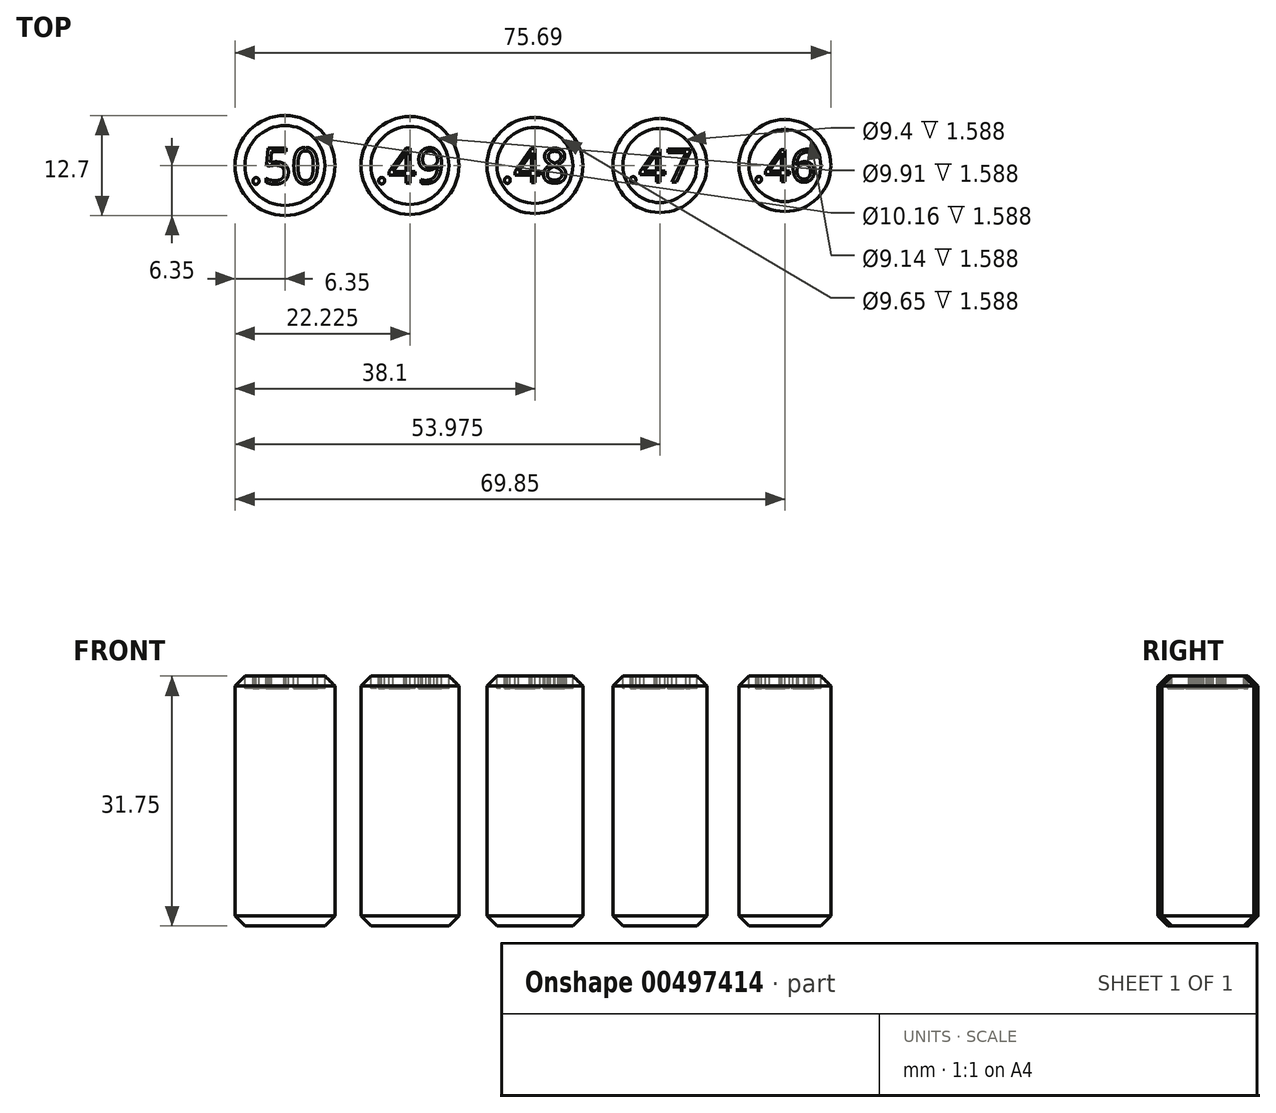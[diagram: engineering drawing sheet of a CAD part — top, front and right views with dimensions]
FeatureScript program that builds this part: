
annotation { "Feature Type Name" : "Feature", "Feature Type Description" : "" }
export const myFeature = defineFeature(function(context is Context, id is Id, definition is map)
    precondition{}
    {
        {
            var Q0;
            Q0=qCreatedBy(makeId("Top.planeOp"),FACE);
            var sketch = newSketch(context, id + "F0", { "sketchPlane" : qUnion([Q0])});
            skCircle(sketch, "E0", {"center": v(-31.75, 0) * mm, "radius": 6.35 * mm});
            skCircle(sketch, "E1", {"center": v(-15.88, 0) * mm, "radius": 6.22 * mm});
            skCircle(sketch, "E2", {"center": v(0, 0) * mm, "radius": 6.1 * mm});
            skCircle(sketch, "E3", {"center": v(15.88, 0) * mm, "radius": 5.97 * mm});
            skCircle(sketch, "E4", {"center": v(31.75, 0) * mm, "radius": 5.84 * mm});
            skSolve(sketch);
        }
        {
            var Q0;
            Q0=makeQuery(id+"F0.imprint","IMPRINT",FACE,{"disambiguationData":[TD([[makeQuery(id+"F0.imprint","IMPRINT",EDGE,{"derivedFrom":sQuery(id+"F0.wireOp",EDGE,"E0")}),1.0]])]});
            var Q1;
            Q1=makeQuery(id+"F0.imprint","IMPRINT",FACE,{"disambiguationData":[TD([[makeQuery(id+"F0.imprint","IMPRINT",EDGE,{"derivedFrom":sQuery(id+"F0.wireOp",EDGE,"E1")}),1.0]])]});
            var Q2;
            Q2=makeQuery(id+"F0.imprint","IMPRINT",FACE,{"disambiguationData":[TD([[makeQuery(id+"F0.imprint","IMPRINT",EDGE,{"derivedFrom":sQuery(id+"F0.wireOp",EDGE,"E2")}),1.0]])]});
            var Q3;
            Q3=makeQuery(id+"F0.imprint","IMPRINT",FACE,{"disambiguationData":[TD([[makeQuery(id+"F0.imprint","IMPRINT",EDGE,{"derivedFrom":sQuery(id+"F0.wireOp",EDGE,"E3")}),1.0]])]});
            var Q4;
            Q4=makeQuery(id+"F0.imprint","IMPRINT",FACE,{"disambiguationData":[TD([[makeQuery(id+"F0.imprint","IMPRINT",EDGE,{"derivedFrom":sQuery(id+"F0.wireOp",EDGE,"E4")}),1.0]])]});
            extrude(context, id + "F1", {"entities" : qUnion([Q0, Q1, Q2, Q3, Q4]), "depth" : 31.75 * mm});
        }
        {
            var Q0;
            Q0=makeQuery(id+"F1.opExtrude","SWEPT_FACE",FACE,{"disambiguationData":[OSD([sQuery(id+"F0.wireOp",EDGE,"E0")])]});
            var Q1;
            Q1=makeQuery(id+"F1.opExtrude","SWEPT_FACE",FACE,{"disambiguationData":[OSD([sQuery(id+"F0.wireOp",EDGE,"E1")])]});
            var Q2;
            Q2=makeQuery(id+"F1.opExtrude","SWEPT_FACE",FACE,{"disambiguationData":[OSD([sQuery(id+"F0.wireOp",EDGE,"E2")])]});
            var Q3;
            Q3=makeQuery(id+"F1.opExtrude","SWEPT_FACE",FACE,{"disambiguationData":[OSD([sQuery(id+"F0.wireOp",EDGE,"E3")])]});
            var Q4;
            Q4=makeQuery(id+"F1.opExtrude","SWEPT_FACE",FACE,{"disambiguationData":[OSD([sQuery(id+"F0.wireOp",EDGE,"E4")])]});
            chamfer(context, id + "F2", {"entities" : qUnion([Q0, Q1, Q2, Q3, Q4]), "width" : 1.27 * mm, "tangentPropagation" : true});
        }
        {
            var Q0;
            Q0=makeQuery(id+"F1.opExtrude","CAP_FACE",FACE,{"disambiguationData":[OSD([sQuery(id+"F0.wireOp",EDGE,"E0")])],"isStart":false});
            var sketch = newSketch(context, id + "F3", { "sketchPlane" : qUnion([Q0])});
            skText(sketch, "E5", { "text": ".50", "fontName": "OpenSans-Regular.ttf"});
            skCircle(sketch, "E6.0", {"center": v(-15.88, 0) * mm, "radius": 4.95 * mm});
            skCircle(sketch, "E7.0", {"center": v(-31.75, 0) * mm, "radius": 5.08 * mm});
            skCircle(sketch, "E8.0", {"center": v(0, 0) * mm, "radius": 4.83 * mm});
            skCircle(sketch, "E9.0", {"center": v(15.88, 0) * mm, "radius": 4.7 * mm});
            skCircle(sketch, "E10.0", {"center": v(31.75, 0) * mm, "radius": 4.57 * mm});
            skText(sketch, "E11", { "text": ".49", "fontName": "OpenSans-Regular.ttf"});
            skText(sketch, "E12", { "text": ".48", "fontName": "OpenSans-Regular.ttf"});
            skText(sketch, "E13", { "text": ".47", "fontName": "OpenSans-Regular.ttf"});
            skText(sketch, "E14", { "text": ".46", "fontName": "OpenSans-Regular.ttf"});
            const initialGuessF3  = {"E5": [-0.03628, -0.0023, 1, 0, 0.00458], "E11": [-0.0203, -0.00224, 1, 0, 0.00448], "E12": [-0.0043, -0.00218, 1, 0, 0.00436], "E13": [0.01168, -0.00212, 1, 0, 0.00424], "E14": [0.02767, -0.00206, 1, 0, 0.00412]};
            skSetInitialGuess(sketch, initialGuessF3);
            skSolve(sketch);
        }
        {
            var Q0;
            Q0=makeQuery(id+"F3.imprint","IMPRINT",FACE,{"disambiguationData":[TD([[makeQuery(id+"F3.imprint","IMPRINT",EDGE,{"derivedFrom":sQuery(id+"F3.wireOp",EDGE,"E5.sketch_text.stroke-0")}),1.0]])]});
            var Q1;
            Q1=makeQuery(id+"F3.imprint","IMPRINT",FACE,{"disambiguationData":[TD([[makeQuery(id+"F3.imprint","IMPRINT",EDGE,{"derivedFrom":sQuery(id+"F3.wireOp",EDGE,"E5.sketch_text.stroke-35")}),1.0]])]});
            var Q2;
            Q2=makeQuery(id+"F3.imprint","IMPRINT",FACE,{"disambiguationData":[TD([[makeQuery(id+"F3.imprint","IMPRINT",EDGE,{"derivedFrom":sQuery(id+"F3.wireOp",EDGE,"E6.0")}),1.0]])]});
            var Q3;
            Q3=makeQuery(id+"F3.imprint","IMPRINT",FACE,{"disambiguationData":[TD([[makeQuery(id+"F3.imprint","IMPRINT",EDGE,{"derivedFrom":sQuery(id+"F3.wireOp",EDGE,"E8.0")}),1.0]])]});
            var Q4;
            Q4=makeQuery(id+"F3.imprint","IMPRINT",FACE,{"disambiguationData":[TD([[makeQuery(id+"F3.imprint","IMPRINT",EDGE,{"derivedFrom":sQuery(id+"F3.wireOp",EDGE,"E9.0")}),1.0]])]});
            var Q5;
            Q5=makeQuery(id+"F3.imprint","IMPRINT",FACE,{"disambiguationData":[TD([[makeQuery(id+"F3.imprint","IMPRINT",EDGE,{"derivedFrom":sQuery(id+"F3.wireOp",EDGE,"E10.0")}),1.0]])]});
            var Q6;
            Q6=makeQuery(id+"F3.imprint","IMPRINT",FACE,{"disambiguationData":[TD([[makeQuery(id+"F3.imprint","IMPRINT",EDGE,{"derivedFrom":sQuery(id+"F3.wireOp",EDGE,"E14.sketch_text.stroke-40")}),1.0]])]});
            var Q7;
            Q7=makeQuery(id+"F3.imprint","IMPRINT",FACE,{"disambiguationData":[TD([[makeQuery(id+"F3.imprint","IMPRINT",EDGE,{"derivedFrom":sQuery(id+"F3.wireOp",EDGE,"E14.sketch_text.stroke-19")}),1.0]])]});
            var Q8;
            Q8=makeQuery(id+"F3.imprint","IMPRINT",FACE,{"disambiguationData":[TD([[makeQuery(id+"F3.imprint","IMPRINT",EDGE,{"derivedFrom":sQuery(id+"F3.wireOp",EDGE,"E13.sketch_text.stroke-19")}),1.0]])]});
            var Q9;
            Q9=makeQuery(id+"F3.imprint","IMPRINT",FACE,{"disambiguationData":[TD([[makeQuery(id+"F3.imprint","IMPRINT",EDGE,{"derivedFrom":sQuery(id+"F3.wireOp",EDGE,"E12.sketch_text.stroke-40")}),1.0]])]});
            var Q10;
            Q10=makeQuery(id+"F3.imprint","IMPRINT",FACE,{"disambiguationData":[TD([[makeQuery(id+"F3.imprint","IMPRINT",EDGE,{"derivedFrom":sQuery(id+"F3.wireOp",EDGE,"E12.sketch_text.stroke-48")}),1.0]])]});
            var Q11;
            Q11=makeQuery(id+"F3.imprint","IMPRINT",FACE,{"disambiguationData":[TD([[makeQuery(id+"F3.imprint","IMPRINT",EDGE,{"derivedFrom":sQuery(id+"F3.wireOp",EDGE,"E12.sketch_text.stroke-19")}),1.0]])]});
            var Q12;
            Q12=makeQuery(id+"F3.imprint","IMPRINT",FACE,{"disambiguationData":[TD([[makeQuery(id+"F3.imprint","IMPRINT",EDGE,{"derivedFrom":sQuery(id+"F3.wireOp",EDGE,"E11.sketch_text.stroke-19")}),1.0]])]});
            var Q13;
            Q13=makeQuery(id+"F3.imprint","IMPRINT",FACE,{"disambiguationData":[TD([[makeQuery(id+"F3.imprint","IMPRINT",EDGE,{"derivedFrom":sQuery(id+"F3.wireOp",EDGE,"E11.sketch_text.stroke-41")}),1.0]])]});
            extrude(context, id + "F4", {"entities" : qUnion([Q0, Q1, Q2, Q3, Q4, Q5, Q6, Q7, Q8, Q9, Q10, Q11, Q12, Q13]), "operationType" : NewBodyOperationType.REMOVE, "oppositeDirection" : true, "depth" : 1.59 * mm, "offsetDistance" : 25.4 * mm});
        }
    });
